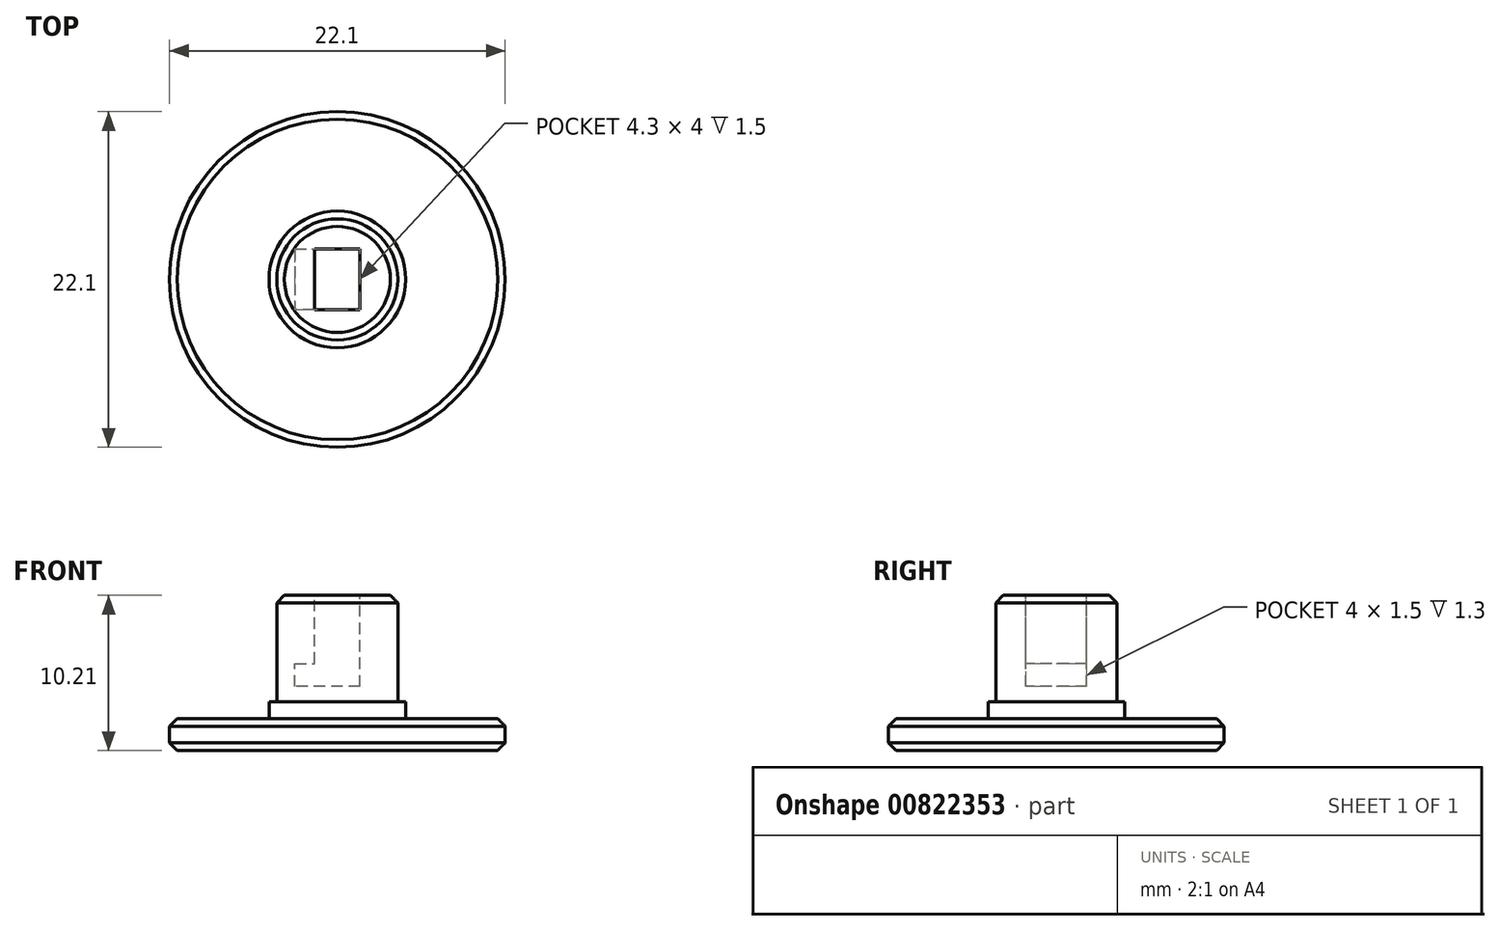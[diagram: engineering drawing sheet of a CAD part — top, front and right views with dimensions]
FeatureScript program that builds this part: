
annotation { "Feature Type Name" : "Feature", "Feature Type Description" : "" }
export const myFeature = defineFeature(function(context is Context, id is Id, definition is map)
    precondition{}
    {
        {
            var Q0;
            Q0=qCreatedBy(makeId("Top.planeOp"),FACE);
            var sketch = newSketch(context, id + "F0", { "sketchPlane" : qUnion([Q0])});
            skCircle(sketch, "E0", {"center": v(0, 0) * mm, "radius": 11.05 * mm});
            skSolve(sketch);
        }
        {
            var Q0;
            Q0=qSketchRegion(id+"F0",true);
            extrude(context, id + "F1", {"entities" : qUnion([Q0]), "depth" : 2.1 * mm, "offsetDistance" : 25 * mm});
        }
        {
            var Q0;
            Q0=makeQuery(id+"F1.opExtrude","CAP_FACE",FACE,{"disambiguationData":[OSD([sQuery(id+"F0.wireOp",EDGE,"E0")])],"isStart":false});
            var sketch = newSketch(context, id + "F2", { "sketchPlane" : qUnion([Q0])});
            skCircle(sketch, "E1", {"center": v(0, 0) * mm, "radius": 4.5 * mm});
            skSolve(sketch);
        }
        {
            var Q0;
            Q0=makeQuery(id+"F2.imprint","IMPRINT",FACE,{"disambiguationData":[TD([[makeQuery(id+"F2.imprint","IMPRINT",EDGE,{"derivedFrom":sQuery(id+"F2.wireOp",EDGE,"E1")}),1.0]])]});
            extrude(context, id + "F3", {"entities" : qUnion([Q0]), "operationType" : NewBodyOperationType.ADD, "depth" : 1.11 * mm, "offsetDistance" : 25 * mm});
        }
        {
            var Q0;
            Q0=makeQuery(id+"F3.opExtrude","CAP_FACE",FACE,{"disambiguationData":[OSD([sQuery(id+"F2.wireOp",EDGE,"E1")])],"isStart":false});
            var sketch = newSketch(context, id + "F4", { "sketchPlane" : qUnion([Q0])});
            skCircle(sketch, "E2", {"center": v(0, 0) * mm, "radius": 4 * mm});
            skSolve(sketch);
        }
        {
            var Q0;
            Q0=makeQuery(id+"F4.imprint","IMPRINT",FACE,{"disambiguationData":[TD([[makeQuery(id+"F4.imprint","IMPRINT",EDGE,{"derivedFrom":sQuery(id+"F4.wireOp",EDGE,"E2")}),1.0]])]});
            extrude(context, id + "F5", {"entities" : qUnion([Q0]), "operationType" : NewBodyOperationType.ADD, "depth" : 7 * mm, "offsetDistance" : 25 * mm});
        }
        {
            var Q0;
            Q0=makeQuery(id+"F5.opExtrude","CAP_FACE",FACE,{"disambiguationData":[OSD([sQuery(id+"F4.wireOp",EDGE,"E2")])],"isStart":false});
            var sketch = newSketch(context, id + "F6", { "sketchPlane" : qUnion([Q0])});
            skLineSegment(sketch, "E3.bottom", {"start": v(1.5, 2) * mm, "end": v(-1.5, 2) * mm});
            skLineSegment(sketch, "E3.top", {"start": v(1.5, -2) * mm, "end": v(-1.5, -2) * mm});
            skLineSegment(sketch, "E3.left", {"start": v(1.5, 2) * mm, "end": v(1.5, -2) * mm});
            skLineSegment(sketch, "E3.right", {"start": v(-1.5, 2) * mm, "end": v(-1.5, -2) * mm});
            skPoint(sketch, "E3.middle", {"position": v(0, 0) * mm});
            skSolve(sketch);
        }
        {
            var Q0;
            Q0=makeQuery(id+"F6.imprint","IMPRINT",FACE,{"disambiguationData":[TD([[makeQuery(id+"F6.imprint","IMPRINT",EDGE,{"derivedFrom":sQuery(id+"F6.wireOp",EDGE,"E3.bottom")}),1.0]])]});
            extrude(context, id + "F7", {"entities" : qUnion([Q0]), "operationType" : NewBodyOperationType.REMOVE, "oppositeDirection" : true, "depth" : 6 * mm, "offsetDistance" : 25 * mm});
        }
        {
            var Q0;
            Q0=makeQuery(id+"F7.boolean.opBoolean","COPY",FACE,{"derivedFrom":makeQuery(id+"F7.opExtrude","SWEPT_FACE",FACE,{"disambiguationData":[OSD([sQuery(id+"F6.wireOp",EDGE,"E3.right")])]})});
            var sketch = newSketch(context, id + "F8", { "sketchPlane" : qUnion([Q0])});
            skLineSegment(sketch, "E4.bottom", {"start": v(2, 4.2) * mm, "end": v(-2, 4.2) * mm});
            skLineSegment(sketch, "E4.top", {"start": v(2, 5.7) * mm, "end": v(-2, 5.7) * mm});
            skLineSegment(sketch, "E4.left", {"start": v(2, 4.2) * mm, "end": v(2, 5.7) * mm});
            skLineSegment(sketch, "E4.right", {"start": v(-2, 4.2) * mm, "end": v(-2, 5.7) * mm});
            skSolve(sketch);
        }
        {
            var Q0;
            Q0=makeQuery(id+"F8.imprint","IMPRINT",FACE,{"disambiguationData":[TD([[makeQuery(id+"F8.imprint","IMPRINT",EDGE,{"derivedFrom":sQuery(id+"F8.wireOp",EDGE,"E4.bottom")}),-1.0]])]});
            extrude(context, id + "F9", {"entities" : qUnion([Q0]), "operationType" : NewBodyOperationType.REMOVE, "oppositeDirection" : true, "depth" : 1.3 * mm, "offsetDistance" : 25 * mm});
        }
        {
            var Q0;
            Q0=makeQuery(id+"F9.boolean.opBoolean","COPY",EDGE,{"derivedFrom":makeQuery(id+"F9.opExtrude","CAP_EDGE",EDGE,{"disambiguationData":[OSD([sQuery(id+"F8.wireOp",EDGE,"E4.top")])],"isStart":true})});
            var Q1;
            Q1=makeQuery(id+"F7.boolean.opBoolean","COPY",EDGE,{"derivedFrom":makeQuery(id+"F7.opExtrude","CAP_EDGE",EDGE,{"disambiguationData":[OSD([sQuery(id+"F6.wireOp",EDGE,"E3.bottom")])],"isStart":true})});
            var Q2;
            Q2=makeQuery(id+"F7.boolean.opBoolean","COPY",EDGE,{"derivedFrom":makeQuery(id+"F7.opExtrude","CAP_EDGE",EDGE,{"disambiguationData":[OSD([sQuery(id+"F6.wireOp",EDGE,"E3.right")])],"isStart":true})});
            var Q3;
            Q3=makeQuery(id+"F7.boolean.opBoolean","COPY",EDGE,{"derivedFrom":makeQuery(id+"F7.opExtrude","CAP_EDGE",EDGE,{"disambiguationData":[OSD([sQuery(id+"F6.wireOp",EDGE,"E3.left")])],"isStart":true})});
            var Q4;
            Q4=makeQuery(id+"F7.boolean.opBoolean","COPY",EDGE,{"derivedFrom":makeQuery(id+"F7.opExtrude","CAP_EDGE",EDGE,{"disambiguationData":[OSD([sQuery(id+"F6.wireOp",EDGE,"E3.top")])],"isStart":true})});
            var Q5;
            Q5=makeQuery(id+"F5.opExtrude","CAP_EDGE",EDGE,{"disambiguationData":[OSD([sQuery(id+"F4.wireOp",EDGE,"E2")])],"isStart":false});
            var Q6;
            Q6=makeQuery(id+"F1.opExtrude","CAP_EDGE",EDGE,{"disambiguationData":[OSD([sQuery(id+"F0.wireOp",EDGE,"E0")])],"isStart":true});
            var Q7;
            Q7=makeQuery(id+"F1.opExtrude","CAP_EDGE",EDGE,{"disambiguationData":[OSD([sQuery(id+"F0.wireOp",EDGE,"E0")])],"isStart":false});
            chamfer(context, id + "F10", {"entities" : qUnion([Q0, Q1, Q2, Q3, Q4, Q5, Q6, Q7]), "width" : .5 * mm, "tangentPropagation" : true});
        }
    });
